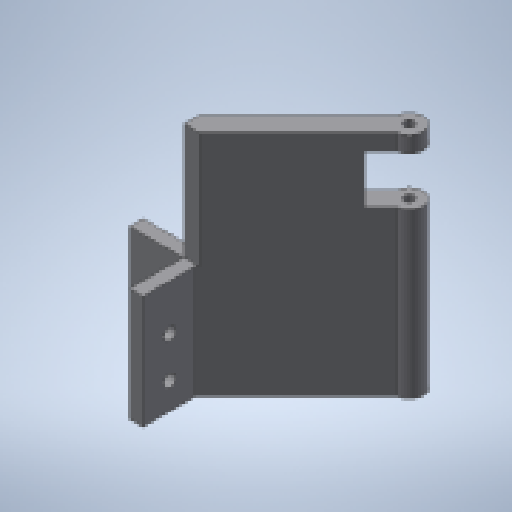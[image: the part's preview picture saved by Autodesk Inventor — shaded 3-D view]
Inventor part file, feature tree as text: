
AUTODESK INVENTOR PART (.ipt)
format: ipt  version: 2023 (Build 270158000, 158)  size: 268,800 bytes
history: native  units: mm
features: extrude x10, sketch x10, projected_geometry x2, plane x1
ambient origin geometry x8: Origin, YZ Plane, XZ Plane, XY Plane, X Axis, Y Axis, Z Axis, Center Point
bodies: Solid1 (feature_tree)
feature tree (23):
  extrude  "Extrusion1"  Depth=20.0mm
  plane  "Work Plane1"
  sketch  "Sketch3"  dims[d2=5.0mm d3=5.0mm]
  extrude  "Extrusion3"  Depth=5.0mm
  extrude  "Extrusion5"  Depth=42.0mm
  sketch  "Sketch8"  dims[d8=42.0mm d9=3.7mm]
  extrude  "Extrusion8"  Depth=42.0mm
  extrude  "Extrusion9"  Depth=25.0mm
  extrude  "Extrusion10"  Depth=5.0mm
  extrude  "Extrusion12"  Depth=55.0mm TaperAngle=0.0deg
  sketch  "Sketch13"  dims[d40=4.5mm d41=10.0mm]
  sketch  "Sketch14"  dims[d42=10.0mm d43=4.5mm]
  extrude  "Extrusion13"  Depth=10.0mm
  extrude  "Extrusion14"  Depth=10.0mm
  extrude  "Extrusion15"  Depth=55.0mm
  sketch  "Sketch1"  dims[d0=20.0mm d1=20.0mm]
  sketch  "Sketch5"  dims[d5=30.0mm d6=0.0mm d7=42.0mm]
  projected_geometry  "Projected Loop2"
  sketch  "Sketch9"  dims[d10=-6.0mm d13=25.0mm]
  sketch  "Sketch10"  dims[d16=18.0mm d17=0.0mm d18=5.0mm]
  sketch  "Sketch12"  dims[d19=135.0deg d22=55.0mm d23=0.0mm]
  sketch  "Sketch15"  dims[d44=10.0mm d45=15.0mm d46=10.0mm d47=10.0mm d48=10.0mm d49=15.0mm d50=4.5mm d51=4.5mm d52=20.0mm d53=0.0mm d54=20.0mm d55=0.0mm d56=135.0deg d58=48.0mm d59=0.0mm d65=0.2mm d66=0.2mm d67=8.0mm d68=5.0mm d70=50.0mm d71=50.0mm d72=20.0mm d73=0.0mm d75=0.0mm d76=5.0mm d77=10.0mm d78=5.0mm d79=4.5mm d80=5.0mm d81=4.5mm d82=10.0mm d83=20.0mm d84=0.0mm d85=20.0mm d86=0.0mm d87=55.0mm d88=0.0mm d63=0.5mm d64=0.872665mm]
  projected_geometry  "Projected Loop3"
